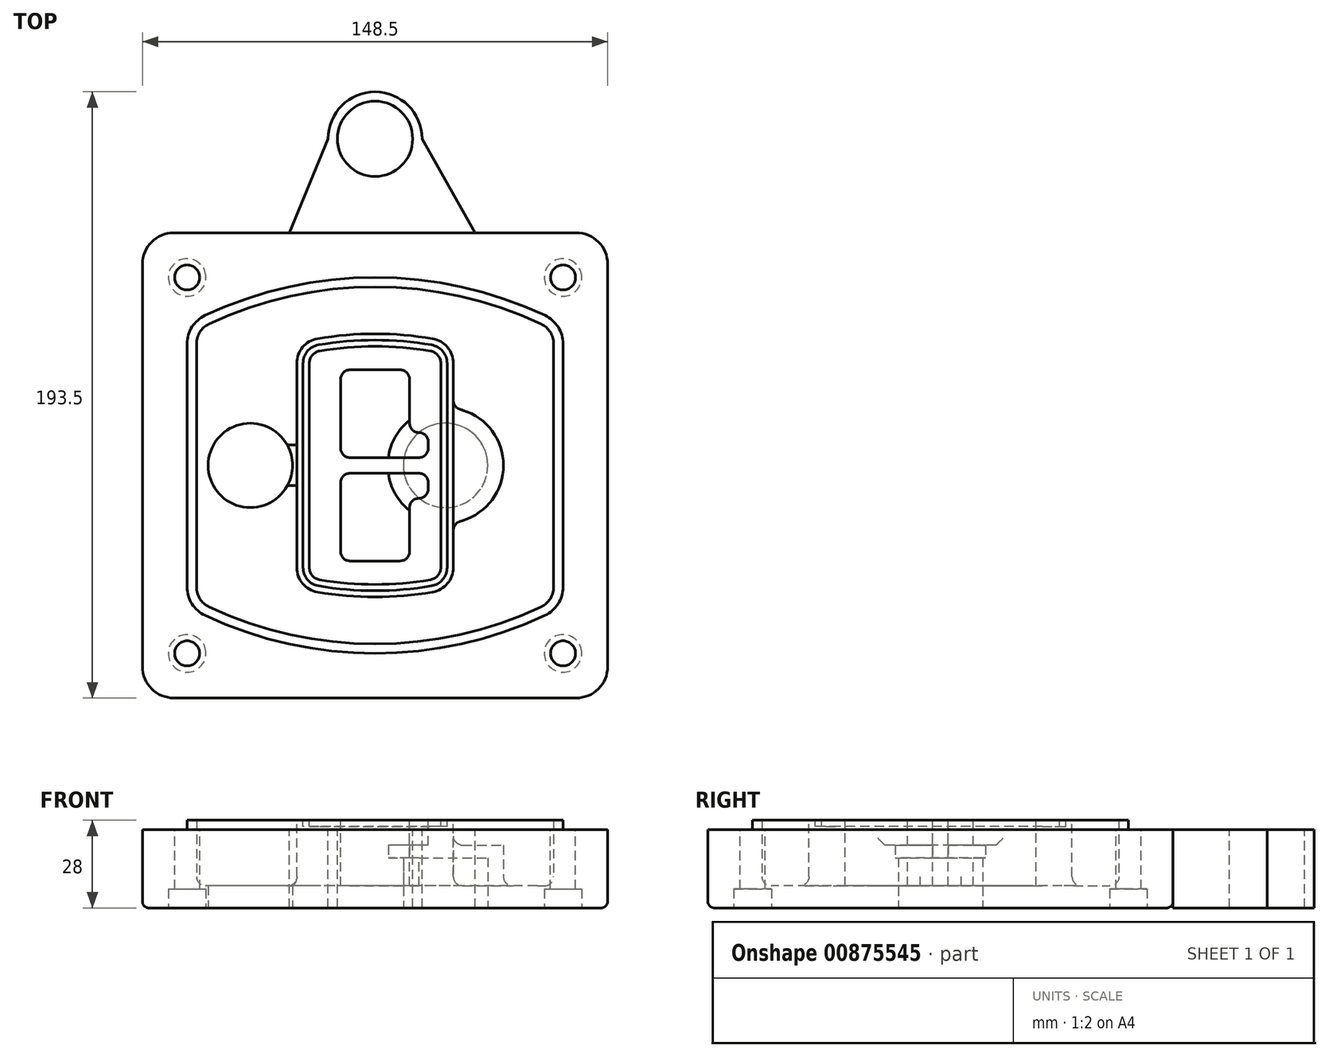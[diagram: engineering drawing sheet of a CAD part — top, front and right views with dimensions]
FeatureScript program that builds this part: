
annotation { "Feature Type Name" : "Feature", "Feature Type Description" : "" }
export const myFeature = defineFeature(function(context is Context, id is Id, definition is map)
    precondition{}
    {
        {
            var Q0;
            Q0=qCreatedBy(makeId("Top.planeOp"),FACE);
            var sketch = newSketch(context, id + "F0", { "sketchPlane" : qUnion([Q0])});
            skPoint(sketch, "E0.rect.middle", {"position": v(0, 0) * mm});
            skLineSegment(sketch, "E1.bottom", {"start": v(-64.25, -74.25) * mm, "end": v(64.25, -74.25) * mm});
            skLineSegment(sketch, "E1.top", {"start": v(-64.25, 74.25) * mm, "end": v(64.25, 74.25) * mm});
            skLineSegment(sketch, "E1.left", {"start": v(-74.25, -64.25) * mm, "end": v(-74.25, 64.25) * mm});
            skLineSegment(sketch, "E1.right", {"start": v(74.25, -64.25) * mm, "end": v(74.25, 64.25) * mm});
            skLineSegment(sketch, "E2", {"start": v(-74.25, 74.25) * mm, "end": v(74.25, -74.25) * mm, "construction": true});
            skLineSegment(sketch, "E3", {"start": v(74.25, 74.25) * mm, "end": v(-74.25, -74.25) * mm, "construction": true});
            skCircle(sketch, "E4", {"center": v(-60, 60) * mm, "radius": 4 * mm});
            skCircle(sketch, "E5", {"center": v(60, 60) * mm, "radius": 4 * mm});
            skCircle(sketch, "E6", {"center": v(60, -60) * mm, "radius": 4 * mm});
            skCircle(sketch, "E7", {"center": v(-60, -60) * mm, "radius": 4 * mm});
            skLineSegment(sketch, "E8", {"start": v(-60, 60) * mm, "end": v(60, 60) * mm, "construction": true});
            skLineSegment(sketch, "E9", {"start": v(60, 60) * mm, "end": v(60, -60) * mm, "construction": true});
            skLineSegment(sketch, "E10", {"start": v(60, -60) * mm, "end": v(-60, -60) * mm, "construction": true});
            skLineSegment(sketch, "E11", {"start": v(-60, -60) * mm, "end": v(-60, 60) * mm, "construction": true});
            skLineSegment(sketch, "E12", {"start": v(-60, 38.83) * mm, "end": v(-60, -38.83) * mm});
            skLineSegment(sketch, "E13", {"start": v(60, 38.83) * mm, "end": v(60, -38.83) * mm});
            skArc(sketch, "E14", {"start": v(54.26, 47.88) * mm, "mid": v(0, 60) * mm, "end": v(-54.26, 47.88) * mm});
            skArc(sketch, "E15", {"start": v(-54.26, -47.88) * mm, "mid": v(0, -60) * mm, "end": v(54.26, -47.88) * mm});
            skLineSegment(sketch, "E16", {"start": v(-60, 0) * mm, "end": v(60, 0) * mm, "construction": true});
            skPoint(sketch, "E17.visualSharp", {"position": v(-60, -45) * mm});
            skArc(sketch, "E17.filletArc", {"start": v(-60, -38.83) * mm, "mid": v(-58.44, -44.2) * mm, "end": v(-54.26, -47.88) * mm});
            skPoint(sketch, "E18.visualSharp", {"position": v(-60, 45) * mm});
            skArc(sketch, "E18.filletArc", {"start": v(-54.26, 47.88) * mm, "mid": v(-58.44, 44.2) * mm, "end": v(-60, 38.83) * mm});
            skPoint(sketch, "E19.visualSharp", {"position": v(60, 45) * mm});
            skArc(sketch, "E19.filletArc", {"start": v(60, 38.83) * mm, "mid": v(58.44, 44.2) * mm, "end": v(54.26, 47.88) * mm});
            skPoint(sketch, "E20.visualSharp", {"position": v(60, -45) * mm});
            skArc(sketch, "E20.filletArc", {"start": v(54.26, -47.88) * mm, "mid": v(58.44, -44.2) * mm, "end": v(60, -38.83) * mm});
            skPoint(sketch, "E21.visualSharp", {"position": v(-74.25, 74.25) * mm});
            skArc(sketch, "E21.filletArc", {"start": v(-64.25, 74.25) * mm, "mid": v(-71.32, 71.32) * mm, "end": v(-74.25, 64.25) * mm});
            skPoint(sketch, "E22.visualSharp", {"position": v(74.25, 74.25) * mm});
            skArc(sketch, "E22.filletArc", {"start": v(74.25, 64.25) * mm, "mid": v(71.32, 71.32) * mm, "end": v(64.25, 74.25) * mm});
            skPoint(sketch, "E23.visualSharp", {"position": v(74.25, -74.25) * mm});
            skArc(sketch, "E23.filletArc", {"start": v(64.25, -74.25) * mm, "mid": v(71.32, -71.32) * mm, "end": v(74.25, -64.25) * mm});
            skPoint(sketch, "E24.visualSharp", {"position": v(-74.25, -74.25) * mm});
            skArc(sketch, "E24.filletArc", {"start": v(-74.25, -64.25) * mm, "mid": v(-71.32, -71.32) * mm, "end": v(-64.25, -74.25) * mm});
            skArc(sketch, "E25.0", {"start": v(57, 38.83) * mm, "mid": v(55.9, 42.58) * mm, "end": v(52.98, 45.17) * mm});
            skLineSegment(sketch, "E25.1", {"start": v(57, 38.83) * mm, "end": v(57, -38.83) * mm});
            skArc(sketch, "E25.2", {"start": v(52.98, -45.17) * mm, "mid": v(55.9, -42.58) * mm, "end": v(57, -38.83) * mm});
            skArc(sketch, "E25.3", {"start": v(-52.98, -45.17) * mm, "mid": v(0, -57) * mm, "end": v(52.98, -45.17) * mm});
            skArc(sketch, "E25.4", {"start": v(-57, -38.83) * mm, "mid": v(-55.9, -42.58) * mm, "end": v(-52.98, -45.17) * mm});
            skArc(sketch, "E25.5", {"start": v(52.98, 45.17) * mm, "mid": v(0, 57) * mm, "end": v(-52.98, 45.17) * mm});
            skLineSegment(sketch, "E25.6", {"start": v(-57, 38.83) * mm, "end": v(-57, -38.83) * mm});
            skArc(sketch, "E25.7", {"start": v(-52.98, 45.17) * mm, "mid": v(-55.9, 42.58) * mm, "end": v(-57, 38.83) * mm});
            skArc(sketch, "E26.0", {"start": v(-55.96, 51.5) * mm, "mid": v(-61.82, 46.33) * mm, "end": v(-64, 38.83) * mm});
            skArc(sketch, "E26.1", {"start": v(55.96, 51.5) * mm, "mid": v(0, 64) * mm, "end": v(-55.96, 51.5) * mm});
            skArc(sketch, "E26.2", {"start": v(64, 38.83) * mm, "mid": v(61.82, 46.33) * mm, "end": v(55.96, 51.5) * mm});
            skLineSegment(sketch, "E26.3", {"start": v(64, 38.83) * mm, "end": v(64, -38.83) * mm});
            skArc(sketch, "E26.4", {"start": v(55.96, -51.5) * mm, "mid": v(61.82, -46.33) * mm, "end": v(64, -38.83) * mm});
            skLineSegment(sketch, "E26.5", {"start": v(-64, 38.83) * mm, "end": v(-64, -38.83) * mm});
            skArc(sketch, "E26.6", {"start": v(-55.96, -51.5) * mm, "mid": v(0, -64) * mm, "end": v(55.96, -51.5) * mm});
            skArc(sketch, "E26.7", {"start": v(-64, -38.83) * mm, "mid": v(-61.82, -46.33) * mm, "end": v(-55.96, -51.5) * mm});
            skSolve(sketch);
        }
        {
            var Q0;
            Q0=makeQuery(id+"F0.imprint","IMPRINT",FACE,{"disambiguationData":[TD([[makeQuery(id+"F0.imprint","IMPRINT",EDGE,{"derivedFrom":sQuery(id+"F0.wireOp",EDGE,"E1.bottom")}),1.0]])]});
            var Q1;
            Q1=makeQuery(id+"F0.imprint","IMPRINT",FACE,{"disambiguationData":[TD([[makeQuery(id+"F0.imprint","IMPRINT",EDGE,{"derivedFrom":sQuery(id+"F0.wireOp",EDGE,"E12")}),1.0]])]});
            var Q2;
            Q2=makeQuery(id+"F0.imprint","IMPRINT",FACE,{"disambiguationData":[TD([[makeQuery(id+"F0.imprint","IMPRINT",EDGE,{"derivedFrom":sQuery(id+"F0.wireOp",EDGE,"E25.0")}),1.0]])]});
            var Q3;
            Q3=makeQuery(id+"F0.imprint","IMPRINT",FACE,{"disambiguationData":[TD([[makeQuery(id+"F0.imprint","IMPRINT",EDGE,{"derivedFrom":sQuery(id+"F0.wireOp",EDGE,"E12")}),-1.0]])]});
            extrude(context, id + "F1", {"entities" : qUnion([Q0, Q1, Q2, Q3]), "oppositeDirection" : true, "depth" : 25 * mm});
        }
        {
            var Q0;
            Q0=makeQuery(id+"F0.imprint","IMPRINT",FACE,{"disambiguationData":[TD([[makeQuery(id+"F0.imprint","IMPRINT",EDGE,{"derivedFrom":sQuery(id+"F0.wireOp",EDGE,"E12")}),1.0]])]});
            extrude(context, id + "F2", {"entities" : qUnion([Q0]), "operationType" : NewBodyOperationType.ADD, "depth" : 3 * mm});
        }
        {
            var Q0;
            Q0=makeQuery(id+"F0.imprint","IMPRINT",FACE,{"disambiguationData":[TD([[makeQuery(id+"F0.imprint","IMPRINT",EDGE,{"derivedFrom":sQuery(id+"F0.wireOp",EDGE,"E25.0")}),1.0]])]});
            extrude(context, id + "F3", {"entities" : qUnion([Q0]), "operationType" : NewBodyOperationType.REMOVE, "oppositeDirection" : true, "depth" : 18 * mm});
        }
        {
            var Q0;
            Q0=makeQuery(id+"F2.opExtrude","CAP_FACE",FACE,{"disambiguationData":[OSD([sQuery(id+"F0.wireOp",EDGE,"E12"),sQuery(id+"F0.wireOp",EDGE,"E13"),sQuery(id+"F0.wireOp",EDGE,"E14"),sQuery(id+"F0.wireOp",EDGE,"E15"),sQuery(id+"F0.wireOp",EDGE,"E17.filletArc"),sQuery(id+"F0.wireOp",EDGE,"E18.filletArc"),sQuery(id+"F0.wireOp",EDGE,"E19.filletArc"),sQuery(id+"F0.wireOp",EDGE,"E20.filletArc"),sQuery(id+"F0.wireOp",EDGE,"E25.0"),sQuery(id+"F0.wireOp",EDGE,"E25.1"),sQuery(id+"F0.wireOp",EDGE,"E25.2"),sQuery(id+"F0.wireOp",EDGE,"E25.3"),sQuery(id+"F0.wireOp",EDGE,"E25.4"),sQuery(id+"F0.wireOp",EDGE,"E25.5"),sQuery(id+"F0.wireOp",EDGE,"E25.6"),sQuery(id+"F0.wireOp",EDGE,"E25.7")])],"isStart":false});
            var sketch = newSketch(context, id + "F4", { "sketchPlane" : qUnion([Q0])});
            skArc(sketch, "E27.0", {"start": v(-18.34, -40.45) * mm, "mid": v(0, -42) * mm, "end": v(18.34, -40.45) * mm});
            skArc(sketch, "E28.0", {"start": v(18.34, 40.45) * mm, "mid": v(0, 42) * mm, "end": v(-18.34, 40.45) * mm});
            skLineSegment(sketch, "E29", {"start": v(-25, 32.57) * mm, "end": v(-25, -32.57) * mm});
            skLineSegment(sketch, "E30", {"start": v(25, 32.57) * mm, "end": v(25, -32.57) * mm});
            skLineSegment(sketch, "E31", {"start": v(-25, 39.1) * mm, "end": v(25, 39.1) * mm, "construction": true});
            skLineSegment(sketch, "E32", {"start": v(-25, -39.1) * mm, "end": v(25, -39.1) * mm, "construction": true});
            skPoint(sketch, "E33.visualSharp", {"position": v(-25, 39.1) * mm});
            skArc(sketch, "E33.filletArc", {"start": v(-18.34, 40.45) * mm, "mid": v(-23.11, 37.73) * mm, "end": v(-25, 32.57) * mm});
            skPoint(sketch, "E34.visualSharp", {"position": v(25, 39.1) * mm});
            skArc(sketch, "E34.filletArc", {"start": v(25, 32.57) * mm, "mid": v(23.11, 37.73) * mm, "end": v(18.34, 40.45) * mm});
            skPoint(sketch, "E35.visualSharp", {"position": v(25, -39.1) * mm});
            skArc(sketch, "E35.filletArc", {"start": v(18.34, -40.45) * mm, "mid": v(23.11, -37.73) * mm, "end": v(25, -32.57) * mm});
            skPoint(sketch, "E36.visualSharp", {"position": v(-25, -39.1) * mm});
            skArc(sketch, "E36.filletArc", {"start": v(-25, -32.57) * mm, "mid": v(-23.11, -37.73) * mm, "end": v(-18.34, -40.45) * mm});
            skArc(sketch, "E37.0", {"start": v(52.98, 45.17) * mm, "mid": v(0, 57) * mm, "end": v(-52.98, 45.17) * mm});
            skArc(sketch, "E37.1", {"start": v(-52.98, 45.17) * mm, "mid": v(-55.9, 42.58) * mm, "end": v(-57, 38.83) * mm});
            skLineSegment(sketch, "E37.2", {"start": v(-57, 38.83) * mm, "end": v(-57, -38.83) * mm});
            skArc(sketch, "E37.3", {"start": v(-57, -38.83) * mm, "mid": v(-55.9, -42.58) * mm, "end": v(-52.98, -45.17) * mm});
            skArc(sketch, "E37.4", {"start": v(-52.98, -45.17) * mm, "mid": v(0, -57) * mm, "end": v(52.98, -45.17) * mm});
            skArc(sketch, "E37.5", {"start": v(52.98, -45.17) * mm, "mid": v(55.9, -42.58) * mm, "end": v(57, -38.83) * mm});
            skLineSegment(sketch, "E37.6", {"start": v(57, 38.83) * mm, "end": v(57, -38.83) * mm});
            skArc(sketch, "E37.7", {"start": v(57, 38.83) * mm, "mid": v(55.9, 42.58) * mm, "end": v(52.98, 45.17) * mm});
            skLineSegment(sketch, "E38.0", {"start": v(23, 32.57) * mm, "end": v(23, -32.57) * mm});
            skArc(sketch, "E38.1", {"start": v(18, -38.48) * mm, "mid": v(21.58, -36.44) * mm, "end": v(23, -32.57) * mm});
            skArc(sketch, "E38.2", {"start": v(-18, -38.48) * mm, "mid": v(0, -40) * mm, "end": v(18, -38.48) * mm});
            skArc(sketch, "E38.3", {"start": v(-23, -32.57) * mm, "mid": v(-21.58, -36.44) * mm, "end": v(-18, -38.48) * mm});
            skLineSegment(sketch, "E38.4", {"start": v(-23, 32.57) * mm, "end": v(-23, -32.57) * mm});
            skArc(sketch, "E38.5", {"start": v(23, 32.57) * mm, "mid": v(21.58, 36.44) * mm, "end": v(18, 38.48) * mm});
            skArc(sketch, "E38.6", {"start": v(-18, 38.48) * mm, "mid": v(-21.58, 36.44) * mm, "end": v(-23, 32.57) * mm});
            skArc(sketch, "E38.7", {"start": v(18, 38.48) * mm, "mid": v(0, 40) * mm, "end": v(-18, 38.48) * mm});
            skArc(sketch, "E39.0", {"start": v(21, 32.57) * mm, "mid": v(20.06, 35.15) * mm, "end": v(17.67, 36.5) * mm});
            skLineSegment(sketch, "E39.1", {"start": v(21, 32.57) * mm, "end": v(21, -32.57) * mm});
            skArc(sketch, "E39.2", {"start": v(17.67, -36.5) * mm, "mid": v(20.06, -35.15) * mm, "end": v(21, -32.57) * mm});
            skArc(sketch, "E39.3", {"start": v(-17.67, -36.5) * mm, "mid": v(0, -38) * mm, "end": v(17.67, -36.5) * mm});
            skArc(sketch, "E39.4", {"start": v(-21, -32.57) * mm, "mid": v(-20.06, -35.15) * mm, "end": v(-17.67, -36.5) * mm});
            skArc(sketch, "E39.5", {"start": v(17.67, 36.5) * mm, "mid": v(0, 38) * mm, "end": v(-17.67, 36.5) * mm});
            skLineSegment(sketch, "E39.6", {"start": v(-21, 32.57) * mm, "end": v(-21, -32.57) * mm});
            skArc(sketch, "E39.7", {"start": v(-17.67, 36.5) * mm, "mid": v(-20.06, 35.15) * mm, "end": v(-21, 32.57) * mm});
            skLineSegment(sketch, "E40", {"start": v(-25, 0) * mm, "end": v(25, 0) * mm, "construction": true});
            skLineSegment(sketch, "E41", {"start": v(-11, 5.5) * mm, "end": v(-11, 27.5) * mm});
            skLineSegment(sketch, "E42", {"start": v(-8, 30.5) * mm, "end": v(8, 30.5) * mm});
            skLineSegment(sketch, "E43", {"start": v(11, 27.5) * mm, "end": v(11, 13.5) * mm});
            skLineSegment(sketch, "E44", {"start": v(14, 10.5) * mm, "end": v(14, 10.5) * mm});
            skLineSegment(sketch, "E45", {"start": v(17, 7.5) * mm, "end": v(17, 5.5) * mm});
            skLineSegment(sketch, "E46", {"start": v(14, 2.5) * mm, "end": v(-8, 2.5) * mm});
            skPoint(sketch, "E47.visualSharp", {"position": v(-11, 30.5) * mm});
            skArc(sketch, "E47.filletArc", {"start": v(-8, 30.5) * mm, "mid": v(-10.12, 29.62) * mm, "end": v(-11, 27.5) * mm});
            skPoint(sketch, "E48.visualSharp", {"position": v(11, 30.5) * mm});
            skArc(sketch, "E48.filletArc", {"start": v(11, 27.5) * mm, "mid": v(10.12, 29.62) * mm, "end": v(8, 30.5) * mm});
            skPoint(sketch, "E49.visualSharp", {"position": v(11, 10.5) * mm});
            skArc(sketch, "E49.filletArc", {"start": v(11, 13.5) * mm, "mid": v(11.88, 11.38) * mm, "end": v(14, 10.5) * mm});
            skPoint(sketch, "E50.visualSharp", {"position": v(17, 10.5) * mm});
            skArc(sketch, "E50.filletArc", {"start": v(17, 7.5) * mm, "mid": v(16.12, 9.62) * mm, "end": v(14, 10.5) * mm});
            skPoint(sketch, "E51.visualSharp", {"position": v(17, 2.5) * mm});
            skArc(sketch, "E51.filletArc", {"start": v(14, 2.5) * mm, "mid": v(16.12, 3.38) * mm, "end": v(17, 5.5) * mm});
            skPoint(sketch, "E52.visualSharp", {"position": v(-11, 2.5) * mm});
            skArc(sketch, "E52.filletArc", {"start": v(-11, 5.5) * mm, "mid": v(-10.12, 3.38) * mm, "end": v(-8, 2.5) * mm});
            skLineSegment(sketch, "E53.0.MirrorCS", {"start": v(14, -2.5) * mm, "end": v(-8, -2.5) * mm});
            skArc(sketch, "E54.0.MirrorCS", {"start": v(-11, -5.5) * mm, "mid": v(-10.12, -3.38) * mm, "end": v(-8, -2.5) * mm});
            skLineSegment(sketch, "E55.0.MirrorCS", {"start": v(-11, -5.5) * mm, "end": v(-11, -27.5) * mm});
            skArc(sketch, "E56.0.MirrorCS", {"start": v(-8, -30.5) * mm, "mid": v(-10.12, -29.62) * mm, "end": v(-11, -27.5) * mm});
            skLineSegment(sketch, "E57.0.MirrorCS", {"start": v(-8, -30.5) * mm, "end": v(8, -30.5) * mm});
            skArc(sketch, "E58.0.MirrorCS", {"start": v(11, -27.5) * mm, "mid": v(10.12, -29.62) * mm, "end": v(8, -30.5) * mm});
            skLineSegment(sketch, "E59.0.MirrorCS", {"start": v(11, -27.5) * mm, "end": v(11, -13.5) * mm});
            skArc(sketch, "E60.0.MirrorCS", {"start": v(11, -13.5) * mm, "mid": v(11.88, -11.38) * mm, "end": v(14, -10.5) * mm});
            skArc(sketch, "E61.0.MirrorCS", {"start": v(17, -7.5) * mm, "mid": v(16.12, -9.62) * mm, "end": v(14, -10.5) * mm});
            skLineSegment(sketch, "E62.0.MirrorCS", {"start": v(17, -7.5) * mm, "end": v(17, -5.5) * mm});
            skArc(sketch, "E63.0.MirrorCS", {"start": v(14, -2.5) * mm, "mid": v(16.12, -3.38) * mm, "end": v(17, -5.5) * mm});
            skSolve(sketch);
        }
        {
            var Q0;
            Q0=makeQuery(id+"F4.imprint","IMPRINT",FACE,{"disambiguationData":[TD([[makeQuery(id+"F4.imprint","IMPRINT",EDGE,{"derivedFrom":sQuery(id+"F4.wireOp",EDGE,"E27.0")}),1.0]])]});
            var Q1;
            Q1=makeQuery(id+"F4.imprint","IMPRINT",FACE,{"disambiguationData":[TD([[makeQuery(id+"F4.imprint","IMPRINT",EDGE,{"derivedFrom":sQuery(id+"F4.wireOp",EDGE,"E38.0")}),-1.0]])]});
            var Q2;
            Q2=makeQuery(id+"F4.imprint","IMPRINT",FACE,{"disambiguationData":[TD([[makeQuery(id+"F4.imprint","IMPRINT",EDGE,{"derivedFrom":sQuery(id+"F4.wireOp",EDGE,"E39.0")}),1.0]])]});
            extrude(context, id + "F5", {"entities" : qUnion([Q0, Q1, Q2]), "operationType" : NewBodyOperationType.ADD, "endBound" : BoundingType.UP_TO_NEXT, "oppositeDirection" : true, "depth" : 25 * mm});
        }
        {
            var Q0;
            Q0=makeQuery(id+"F4.imprint","IMPRINT",FACE,{"disambiguationData":[TD([[makeQuery(id+"F4.imprint","IMPRINT",EDGE,{"derivedFrom":sQuery(id+"F4.wireOp",EDGE,"E38.0")}),-1.0]])]});
            extrude(context, id + "F6", {"entities" : qUnion([Q0]), "operationType" : NewBodyOperationType.REMOVE, "oppositeDirection" : true, "depth" : 2 * mm});
        }
        {
            var Q0;
            Q0=makeQuery(id+"F1.opExtrude","CAP_FACE",FACE,{"disambiguationData":[OSD([sQuery(id+"F0.wireOp",EDGE,"E1.bottom"),sQuery(id+"F0.wireOp",EDGE,"E1.top"),sQuery(id+"F0.wireOp",EDGE,"E1.left"),sQuery(id+"F0.wireOp",EDGE,"E1.right"),sQuery(id+"F0.wireOp",EDGE,"E4"),sQuery(id+"F0.wireOp",EDGE,"E5"),sQuery(id+"F0.wireOp",EDGE,"E6"),sQuery(id+"F0.wireOp",EDGE,"E7"),sQuery(id+"F0.wireOp",EDGE,"E21.filletArc"),sQuery(id+"F0.wireOp",EDGE,"E22.filletArc"),sQuery(id+"F0.wireOp",EDGE,"E23.filletArc"),sQuery(id+"F0.wireOp",EDGE,"E24.filletArc")])],"isStart":false});
            var sketch = newSketch(context, id + "F7", { "sketchPlane" : qUnion([Q0])});
            skCircle(sketch, "E64", {"center": v(22.5, 0) * mm, "radius": 13.47 * mm});
            skCircle(sketch, "E65", {"center": v(-39.81, 0) * mm, "radius": 13.47 * mm});
            skLineSegment(sketch, "E66", {"start": v(74.25, 0) * mm, "end": v(-74.25, 0) * mm});
            skCircle(sketch, "E67", {"center": v(22.5, 0) * mm, "radius": 18.47 * mm});
            skCircle(sketch, "E68", {"center": v(60, -60) * mm, "radius": 6 * mm});
            skCircle(sketch, "E69", {"center": v(-60, -60) * mm, "radius": 6 * mm});
            skCircle(sketch, "E70", {"center": v(-60, 60) * mm, "radius": 6 * mm});
            skCircle(sketch, "E71", {"center": v(60, 60) * mm, "radius": 6 * mm});
            skSolve(sketch);
        }
        {
            var Q0;
            {var subQ1=sQuery(id+"F7.wireOp",EDGE,"E66");var subQ4=sQuery(id+"F7.wireOp",EDGE,"E64");var subQ6=makeQuery(id+"F7.imprint","INTERSECT",VERTEX,{"disambiguationData":[OD(0.0)],"derivedFrom":[subQ4,subQ1]});Q0=makeQuery(id+"F7.imprint","IMPRINT",FACE,{"disambiguationData":[TD([[makeQuery(id+"F7.imprint","IMPRINT",EDGE,{"disambiguationData":[TD([[subQ6,-1.0]])],"derivedFrom":subQ4}),-1.0]])]});}
            var Q1;
            {var subQ0=sQuery(id+"F7.wireOp",EDGE,"E66");var subQ1=sQuery(id+"F7.wireOp",EDGE,"E64");var subQ3=makeQuery(id+"F7.imprint","INTERSECT",VERTEX,{"disambiguationData":[OD(0.0)],"derivedFrom":[subQ1,subQ0]});Q1=makeQuery(id+"F7.imprint","IMPRINT",FACE,{"disambiguationData":[TD([[makeQuery(id+"F7.imprint","IMPRINT",EDGE,{"disambiguationData":[TD([[subQ3,-1.0]])],"derivedFrom":subQ1}),1.0]])]});}
            var Q2;
            {var subQ0=sQuery(id+"F7.wireOp",EDGE,"E66");var subQ1=sQuery(id+"F7.wireOp",EDGE,"E64");var subQ3=makeQuery(id+"F7.imprint","INTERSECT",VERTEX,{"disambiguationData":[OD(0.0)],"derivedFrom":[subQ1,subQ0]});Q2=makeQuery(id+"F7.imprint","IMPRINT",FACE,{"disambiguationData":[TD([[makeQuery(id+"F7.imprint","IMPRINT",EDGE,{"disambiguationData":[TD([[subQ3,1.0]])],"derivedFrom":subQ1}),1.0]])]});}
            var Q3;
            {var subQ1=sQuery(id+"F7.wireOp",EDGE,"E66");var subQ4=sQuery(id+"F7.wireOp",EDGE,"E64");var subQ6=makeQuery(id+"F7.imprint","INTERSECT",VERTEX,{"disambiguationData":[OD(0.0)],"derivedFrom":[subQ4,subQ1]});Q3=makeQuery(id+"F7.imprint","IMPRINT",FACE,{"disambiguationData":[TD([[makeQuery(id+"F7.imprint","IMPRINT",EDGE,{"disambiguationData":[TD([[subQ6,1.0]])],"derivedFrom":subQ4}),-1.0]])]});}
            extrude(context, id + "F8", {"entities" : qUnion([Q0, Q1, Q2, Q3]), "operationType" : NewBodyOperationType.ADD, "oppositeDirection" : true, "depth" : 20 * mm});
        }
        {
            var Q0;
            {var subQ0=sQuery(id+"F7.wireOp",EDGE,"E66");var subQ1=sQuery(id+"F7.wireOp",EDGE,"E64");var subQ3=makeQuery(id+"F7.imprint","INTERSECT",VERTEX,{"disambiguationData":[OD(0.0)],"derivedFrom":[subQ1,subQ0]});Q0=makeQuery(id+"F7.imprint","IMPRINT",FACE,{"disambiguationData":[TD([[makeQuery(id+"F7.imprint","IMPRINT",EDGE,{"disambiguationData":[TD([[subQ3,-1.0]])],"derivedFrom":subQ1}),1.0]])]});}
            var Q1;
            {var subQ0=sQuery(id+"F7.wireOp",EDGE,"E66");var subQ1=sQuery(id+"F7.wireOp",EDGE,"E64");var subQ3=makeQuery(id+"F7.imprint","INTERSECT",VERTEX,{"disambiguationData":[OD(0.0)],"derivedFrom":[subQ1,subQ0]});Q1=makeQuery(id+"F7.imprint","IMPRINT",FACE,{"disambiguationData":[TD([[makeQuery(id+"F7.imprint","IMPRINT",EDGE,{"disambiguationData":[TD([[subQ3,1.0]])],"derivedFrom":subQ1}),1.0]])]});}
            extrude(context, id + "F9", {"entities" : qUnion([Q0, Q1]), "operationType" : NewBodyOperationType.REMOVE, "oppositeDirection" : true, "depth" : 16 * mm});
        }
        {
            var Q0;
            {var subQ0=sQuery(id+"F7.wireOp",EDGE,"E66");var subQ1=sQuery(id+"F7.wireOp",EDGE,"E65");var subQ3=makeQuery(id+"F7.imprint","INTERSECT",VERTEX,{"disambiguationData":[OD(0.0)],"derivedFrom":[subQ1,subQ0]});Q0=makeQuery(id+"F7.imprint","IMPRINT",FACE,{"disambiguationData":[TD([[makeQuery(id+"F7.imprint","IMPRINT",EDGE,{"disambiguationData":[TD([[subQ3,-1.0]])],"derivedFrom":subQ1}),1.0]])]});}
            var Q1;
            {var subQ0=sQuery(id+"F7.wireOp",EDGE,"E66");var subQ1=sQuery(id+"F7.wireOp",EDGE,"E65");var subQ3=makeQuery(id+"F7.imprint","INTERSECT",VERTEX,{"disambiguationData":[OD(0.0)],"derivedFrom":[subQ1,subQ0]});Q1=makeQuery(id+"F7.imprint","IMPRINT",FACE,{"disambiguationData":[TD([[makeQuery(id+"F7.imprint","IMPRINT",EDGE,{"disambiguationData":[TD([[subQ3,1.0]])],"derivedFrom":subQ1}),1.0]])]});}
            extrude(context, id + "F10", {"entities" : qUnion([Q0, Q1]), "operationType" : NewBodyOperationType.REMOVE, "oppositeDirection" : true, "depth" : 25 * mm});
        }
        {
            var Q0;
            Q0=makeQuery(id+"F7.imprint","IMPRINT",FACE,{"disambiguationData":[TD([[makeQuery(id+"F7.imprint","IMPRINT",EDGE,{"derivedFrom":sQuery(id+"F7.wireOp",EDGE,"E68")}),1.0]])]});
            var Q1;
            Q1=makeQuery(id+"F7.imprint","IMPRINT",FACE,{"disambiguationData":[TD([[makeQuery(id+"F7.imprint","IMPRINT",EDGE,{"derivedFrom":makeQuery(id+"F1.opExtrude","CAP_EDGE",EDGE,{"disambiguationData":[OSD([sQuery(id+"F0.wireOp",EDGE,"E5")])],"isStart":false})}),-1.0]])]});
            var Q2;
            Q2=makeQuery(id+"F7.imprint","IMPRINT",FACE,{"disambiguationData":[TD([[makeQuery(id+"F7.imprint","IMPRINT",EDGE,{"derivedFrom":sQuery(id+"F7.wireOp",EDGE,"E69")}),1.0]])]});
            var Q3;
            Q3=makeQuery(id+"F7.imprint","IMPRINT",FACE,{"disambiguationData":[TD([[makeQuery(id+"F7.imprint","IMPRINT",EDGE,{"derivedFrom":makeQuery(id+"F1.opExtrude","CAP_EDGE",EDGE,{"disambiguationData":[OSD([sQuery(id+"F0.wireOp",EDGE,"E4")])],"isStart":false})}),-1.0]])]});
            var Q4;
            Q4=makeQuery(id+"F7.imprint","IMPRINT",FACE,{"disambiguationData":[TD([[makeQuery(id+"F7.imprint","IMPRINT",EDGE,{"derivedFrom":sQuery(id+"F7.wireOp",EDGE,"E70")}),1.0]])]});
            var Q5;
            Q5=makeQuery(id+"F7.imprint","IMPRINT",FACE,{"disambiguationData":[TD([[makeQuery(id+"F7.imprint","IMPRINT",EDGE,{"derivedFrom":makeQuery(id+"F1.opExtrude","CAP_EDGE",EDGE,{"disambiguationData":[OSD([sQuery(id+"F0.wireOp",EDGE,"E7")])],"isStart":false})}),-1.0]])]});
            var Q6;
            Q6=makeQuery(id+"F7.imprint","IMPRINT",FACE,{"disambiguationData":[TD([[makeQuery(id+"F7.imprint","IMPRINT",EDGE,{"derivedFrom":sQuery(id+"F7.wireOp",EDGE,"E71")}),1.0]])]});
            var Q7;
            Q7=makeQuery(id+"F7.imprint","IMPRINT",FACE,{"disambiguationData":[TD([[makeQuery(id+"F7.imprint","IMPRINT",EDGE,{"derivedFrom":makeQuery(id+"F1.opExtrude","CAP_EDGE",EDGE,{"disambiguationData":[OSD([sQuery(id+"F0.wireOp",EDGE,"E6")])],"isStart":false})}),-1.0]])]});
            extrude(context, id + "F11", {"entities" : qUnion([Q0, Q1, Q2, Q3, Q4, Q5, Q6, Q7]), "operationType" : NewBodyOperationType.REMOVE, "oppositeDirection" : true, "depth" : 6 * mm});
        }
        {
            var Q0;
            Q0=makeQuery(id+"F9.boolean.opBoolean","COPY",FACE,{"derivedFrom":makeQuery(id+"F9.opExtrude","CAP_FACE",FACE,{"disambiguationData":[OSD([sQuery(id+"F7.wireOp",EDGE,"E64")])],"isStart":false})});
            var sketch = newSketch(context, id + "F12", { "sketchPlane" : qUnion([Q0])});
            skArc(sketch, "E72.0", {"start": v(11, 14.45) * mm, "mid": v(6.45, 9.13) * mm, "end": v(4.2, 2.5) * mm});
            skArc(sketch, "E72.1", {"start": v(4.2, -2.5) * mm, "mid": v(6.45, -9.13) * mm, "end": v(11, -14.45) * mm});
            skLineSegment(sketch, "E73", {"start": v(4.2, -2.5) * mm, "end": v(14, -2.5) * mm});
            skLineSegment(sketch, "E74.0", {"start": v(14, 2.5) * mm, "end": v(4.2, 2.5) * mm});
            skArc(sketch, "E74.1", {"start": v(14, 2.5) * mm, "mid": v(16.12, 3.38) * mm, "end": v(17, 5.5) * mm});
            skLineSegment(sketch, "E74.2", {"start": v(17, 7.5) * mm, "end": v(17, 5.5) * mm});
            skArc(sketch, "E74.3", {"start": v(17, 7.5) * mm, "mid": v(16.12, 9.62) * mm, "end": v(14, 10.5) * mm});
            skArc(sketch, "E74.4", {"start": v(11, 13.5) * mm, "mid": v(11.88, 11.38) * mm, "end": v(14, 10.5) * mm});
            skLineSegment(sketch, "E74.5", {"start": v(11, 14.45) * mm, "end": v(11, 13.5) * mm});
            skLineSegment(sketch, "E74.7", {"start": v(14, -2.5) * mm, "end": v(4.2, -2.5) * mm});
            skArc(sketch, "E74.8", {"start": v(14, -2.5) * mm, "mid": v(16.12, -3.38) * mm, "end": v(17, -5.5) * mm});
            skLineSegment(sketch, "E74.9", {"start": v(17, -7.5) * mm, "end": v(17, -5.5) * mm});
            skArc(sketch, "E74.10", {"start": v(17, -7.5) * mm, "mid": v(16.12, -9.62) * mm, "end": v(14, -10.5) * mm});
            skArc(sketch, "E74.11", {"start": v(11, -13.5) * mm, "mid": v(11.88, -11.38) * mm, "end": v(14, -10.5) * mm});
            skLineSegment(sketch, "E74.12", {"start": v(11, -14.45) * mm, "end": v(11, -13.5) * mm});
            skPoint(sketch, "E75.orphan", {"position": v(11, -27.5) * mm});
            skPoint(sketch, "E76.orphan", {"position": v(-8, -2.5) * mm});
            skPoint(sketch, "E77.orphan", {"position": v(-8, 2.5) * mm});
            skPoint(sketch, "E78.orphan", {"position": v(11, 27.5) * mm});
            skSolve(sketch);
        }
        {
            var Q0;
            {var subQ7=sQuery(id+"F12.wireOp",EDGE,"E72.0");var subQ14=sQuery(id+"F12.wireOp",EDGE,"E72.1");var subQ16=sQuery(id+"F12.wireOp",EDGE,"E74.1");var subQ18=sQuery(id+"F12.wireOp",EDGE,"E74.8");Q0=qUnion([makeQuery(id+"F12.imprint","IMPRINT",FACE,{"disambiguationData":[TD([[makeQuery(id+"F12.imprint","IMPRINT",EDGE,{"derivedFrom":subQ7}),1.0]])]}),makeQuery(id+"F12.imprint","IMPRINT",FACE,{"disambiguationData":[TD([[makeQuery(id+"F12.imprint","IMPRINT",EDGE,{"derivedFrom":subQ14}),1.0]])]}),makeQuery(id+"F12.imprint","IMPRINT",FACE,{"disambiguationData":[TD([[makeQuery(id+"F12.imprint","IMPRINT",EDGE,{"derivedFrom":subQ16}),1.0]])]}),makeQuery(id+"F12.imprint","IMPRINT",FACE,{"disambiguationData":[TD([[makeQuery(id+"F12.imprint","IMPRINT",EDGE,{"derivedFrom":subQ18}),-1.0]])]})]);}
            var Q1;
            Q1=makeQuery(id+"F5.boolean.opBoolean","SPLIT",FACE,{"disambiguationData":[TD([makeQuery(id+"F5.opExtrude","SWEPT_FACE",FACE,{"disambiguationData":[OSD([sQuery(id+"F4.wireOp",EDGE,"E41")])]})])],"derivedFrom":makeQuery(id+"F3.boolean.opBoolean","COPY",FACE,{"derivedFrom":makeQuery(id+"F3.opExtrude","CAP_FACE",FACE,{"disambiguationData":[OSD([sQuery(id+"F0.wireOp",EDGE,"E25.0"),sQuery(id+"F0.wireOp",EDGE,"E25.1"),sQuery(id+"F0.wireOp",EDGE,"E25.2"),sQuery(id+"F0.wireOp",EDGE,"E25.3"),sQuery(id+"F0.wireOp",EDGE,"E25.4"),sQuery(id+"F0.wireOp",EDGE,"E25.5"),sQuery(id+"F0.wireOp",EDGE,"E25.6"),sQuery(id+"F0.wireOp",EDGE,"E25.7")])],"isStart":false})})});
            extrude(context, id + "F13", {"entities" : qUnion([Q0]), "operationType" : NewBodyOperationType.REMOVE, "endBound" : BoundingType.UP_TO_SURFACE, "endBoundEntityFace" : qUnion([Q1]), "depth" : 25 * mm});
        }
        {
            var Q0;
            Q0=makeQuery(id+"F3.boolean.opBoolean","COPY",EDGE,{"derivedFrom":makeQuery(id+"F3.opExtrude","CAP_EDGE",EDGE,{"disambiguationData":[OSD([sQuery(id+"F0.wireOp",EDGE,"E25.6")])],"isStart":false})});
            var Q1;
            Q1=makeQuery(id+"F8.boolean.opBoolean","INTERSECT",EDGE,{"derivedFrom":[makeQuery(id+"F5.opExtrude","SWEPT_FACE",FACE,{"disambiguationData":[OSD([sQuery(id+"F4.wireOp",EDGE,"E30")])]}),makeQuery(id+"F8.opExtrude","CAP_FACE",FACE,{"disambiguationData":[OSD([sQuery(id+"F7.wireOp",EDGE,"E67")])],"isStart":false})]});
            var Q2;
            Q2=makeQuery(id+"F8.boolean.opBoolean","INTERSECT",EDGE,{"disambiguationData":[OD(1.0)],"derivedFrom":[makeQuery(id+"F5.opExtrude","SWEPT_FACE",FACE,{"disambiguationData":[OSD([sQuery(id+"F4.wireOp",EDGE,"E30")])]}),makeQuery(id+"F8.opExtrude","SWEPT_FACE",FACE,{"disambiguationData":[OSD([sQuery(id+"F7.wireOp",EDGE,"E67")])]})]});
            var Q3;
            {var subQ0=sQuery(id+"F4.wireOp",EDGE,"E30");Q3=makeQuery(id+"F8.boolean.opBoolean","SPLIT",EDGE,{"disambiguationData":[TD([makeQuery(id+"F5.opExtrude","SWEPT_FACE",FACE,{"disambiguationData":[OSD([sQuery(id+"F4.wireOp",EDGE,"E35.filletArc")])]})])],"derivedFrom":makeQuery(id+"F5.opExtrude","CAP_EDGE",EDGE,{"disambiguationData":[OSD([subQ0])],"isStart":false})});}
            var Q4;
            {var subQ0=sQuery(id+"F0.wireOp",EDGE,"E25.7");var subQ1=sQuery(id+"F0.wireOp",EDGE,"E25.1");var subQ2=sQuery(id+"F0.wireOp",EDGE,"E25.6");var subQ3=sQuery(id+"F0.wireOp",EDGE,"E25.5");var subQ4=sQuery(id+"F0.wireOp",EDGE,"E25.4");var subQ5=sQuery(id+"F0.wireOp",EDGE,"E25.0");var subQ6=sQuery(id+"F0.wireOp",EDGE,"E25.2");var subQ7=sQuery(id+"F0.wireOp",EDGE,"E25.3");Q4=makeQuery(id+"F8.boolean.opBoolean","INTERSECT",EDGE,{"derivedFrom":[makeQuery(id+"F5.boolean.opBoolean","SPLIT",FACE,{"disambiguationData":[TD([makeQuery(id+"F2.opExtrude","SWEPT_FACE",FACE,{"disambiguationData":[OSD([subQ5])]})])],"derivedFrom":makeQuery(id+"F3.boolean.opBoolean","COPY",FACE,{"derivedFrom":makeQuery(id+"F3.opExtrude","CAP_FACE",FACE,{"disambiguationData":[OSD([subQ5,subQ1,subQ6,subQ7,subQ4,subQ3,subQ2,subQ0])],"isStart":false})})}),makeQuery(id+"F8.opExtrude","SWEPT_FACE",FACE,{"disambiguationData":[OSD([sQuery(id+"F7.wireOp",EDGE,"E67")])]})]});}
            var Q5;
            Q5=makeQuery(id+"F8.boolean.opBoolean","INTERSECT",EDGE,{"disambiguationData":[OD(0.0)],"derivedFrom":[makeQuery(id+"F5.opExtrude","SWEPT_FACE",FACE,{"disambiguationData":[OSD([sQuery(id+"F4.wireOp",EDGE,"E30")])]}),makeQuery(id+"F8.opExtrude","SWEPT_FACE",FACE,{"disambiguationData":[OSD([sQuery(id+"F7.wireOp",EDGE,"E67")])]})]});
            fillet(context, id + "F14", {"entities" : qUnion([Q0, Q1, Q2, Q3, Q4, Q5]), "radius" : 3 * mm, "tangentPropagation" : true, "allowEdgeOverflow" : false});
        }
        {
            var Q0;
            Q0=makeQuery(id+"F1.opExtrude","CAP_EDGE",EDGE,{"disambiguationData":[OSD([sQuery(id+"F0.wireOp",EDGE,"E1.bottom")])],"isStart":false});
            fillet(context, id + "F15", {"entities" : qUnion([Q0]), "radius" : 2 * mm, "tangentPropagation" : true, "allowEdgeOverflow" : false});
        }
        {
            var Q0;
            {var subQ0=sQuery(id+"F0.wireOp",EDGE,"E21.filletArc");var subQ1=sQuery(id+"F0.wireOp",EDGE,"E7");var subQ2=sQuery(id+"F0.wireOp",EDGE,"E6");var subQ3=sQuery(id+"F0.wireOp",EDGE,"E5");var subQ4=sQuery(id+"F0.wireOp",EDGE,"E4");var subQ5=sQuery(id+"F0.wireOp",EDGE,"E22.filletArc");var subQ6=sQuery(id+"F0.wireOp",EDGE,"E1.bottom");var subQ7=sQuery(id+"F0.wireOp",EDGE,"E1.right");var subQ8=sQuery(id+"F0.wireOp",EDGE,"E1.top");var subQ9=sQuery(id+"F0.wireOp",EDGE,"E1.left");var subQ10=sQuery(id+"F0.wireOp",EDGE,"E23.filletArc");var subQ11=sQuery(id+"F0.wireOp",EDGE,"E24.filletArc");Q0=makeQuery(id+"F2.boolean.opBoolean","SPLIT",FACE,{"disambiguationData":[TD([makeQuery(id+"F1.opExtrude","SWEPT_FACE",FACE,{"disambiguationData":[OSD([subQ6])]})])],"derivedFrom":makeQuery(id+"F1.opExtrude","CAP_FACE",FACE,{"disambiguationData":[OSD([subQ6,subQ8,subQ9,subQ7,subQ4,subQ3,subQ2,subQ1,subQ0,subQ5,subQ10,subQ11])],"isStart":true})});}
            var sketch = newSketch(context, id + "F16", { "sketchPlane" : qUnion([Q0])});
            skLineSegment(sketch, "E79", {"start": v(0, 74.25) * mm, "end": v(0, 104.25) * mm});
            skCircle(sketch, "E80", {"center": v(0, 104.25) * mm, "radius": 12 * mm});
            skLineSegment(sketch, "E81", {"start": v(-27.3, 74.25) * mm, "end": v(-15, 104.25) * mm});
            skLineSegment(sketch, "E82", {"start": v(31.97, 74.25) * mm, "end": v(15, 104.25) * mm});
            skLineSegment(sketch, "E83", {"start": v(0, 104.25) * mm, "end": v(0, 119.25) * mm, "construction": true});
            skArc(sketch, "E84", {"start": v(15, 104.25) * mm, "mid": v(0, 119.25) * mm, "end": v(-15, 104.25) * mm});
            skLineSegment(sketch, "E85", {"start": v(31.97, 74.25) * mm, "end": v(-27.3, 74.25) * mm});
            skSolve(sketch);
        }
        {
            var Q0;
            Q0=makeQuery(id+"F16.imprint","IMPRINT",FACE,{"disambiguationData":[TD([[makeQuery(id+"F16.imprint","IMPRINT",EDGE,{"derivedFrom":sQuery(id+"F16.wireOp",EDGE,"E80")}),-1.0]])]});
            extrude(context, id + "F17", {"entities" : qUnion([Q0]), "oppositeDirection" : true, "depth" : 25 * mm, "offsetDistance" : 25 * mm});
        }
    });
